# Revit family: 1-HC_RAS_HCL_TOSHIBA_TCTC_PAVPG_10-16
name_source: partatom
category: Mechanical Equipment
revit_build: Autodesk Revit 2017 (Build: 20160225_1515(x64)
units: mm (PartAtom-declared; Revit-internal decimal feet)

## family parameters
Always vertical = Yes
Cut with Voids When Loaded = No
OmniClass Number = 23.75.00.00
OmniClass Title = Climate Control (HVAC)
Part Type = Normal
Room Calculation Point = No
Round Connector Dimension = Use Diameter
Shared = No
Work Plane-Based = No

## types (4) — shared parameters
Compressor Type = Hermetic DC rotary compressor
Compressor detail - Motor output  (kW) = -
Content Supplier URL = www.hcltech.com
Custom = No
Depth (mm) = 300 mm
Drain pipe = -
Duct diameters = -
EMCS = 4
ETIM Article Class = EC001213
Frequency (Hz) = 50Hz
Height (mm) = 630 mm  [stored 2.06693 ft]
Hydronic Supply Diameter (mm) = 6 mm  [stored 0.019685 ft]
MCA (A) = -
MEPcontent Class = HEATPUMP
MOCP (A) = 15
Manufacturer = Toshiba
Manufacturer URL = https://www.toshiba-carrier.co.jp
Operating range - Cooling (°C) = -15 - 46
Operating range - Heating (°C) = -15 - 24
Product Line = TCTC
Red = Colour RGB-250 000 000
Refrigerant information = R32
Revit Version = 2017
Sound pressure dB(A) Cooling/Heating- Low = -
Sound pressure dB(A) Cooling/Heating- Low+ = -
Sound pressure dB(A) Cooling/Heating- Mid = -
Sound pressure dB(A) Cooling/Heating- Mid+ = -
Static pressure = -
URL = https://www.toshiba-carrier.co.jp
Voltage (V) = 220-240V
White = Colour RGB-255 255 255
Width (mm) = 800 mm  [stored 2.62467 ft]

## per-type parameters (varying)
| type | Air filter | Airflow m3/h- Cooling/Heating | Article Description | Description | Energy class | Hydronic Return Diameter (mm) | Pdesigh | Power consumption-Cooling (Kw) | Power consumption-Heating (Kw) | Rated Capacity kW - Cooling/Heating | Rated Power Consumption kW - Cooling/Heating | Rated efficiency - EER / COP | Running current-Cooling (A) | Running current-Heating (A) | Seasonal efficiency - SEER  / SCOP | Sound pressure dB(A) Cooling/Heating- High | Starting current | Weight (Kg) |
| RAS-10PAVPG-E | Plasma ion charger filtration | - | R32 DSK 9 | R32 DSK 9 | A+++ / A+++ | 10 mm  [stored 0.0328084 ft] | 2.5 / 3.0 (Tbiv= -7degC) | 425 | 570 | 2.5 / 3.2 | 0.45 / 0.60 | 5.56 / 5.33 | 2.31 - 2.13 | 3.12 - 2.86 | 10.6 / 5.20 | 46 / 47 |  | 38 |
| RAS-13PAVPG-E | - | - | R32 DSK 9 | R32 DSK 9 | A+++ / A+++ | 10 mm  [stored 0.0328084 ft] | 3.5 / 3.6 (Tbiv= -7degC) | 725 | 770 | 3.5 / 4.0 | 0.75 / 0.80 | 4.67 / 5.00 | 3.43 - 3.15 | 3.73 - 3.39 | 9.50 / 5.10 | 48 / 50 | - | 38 |
| RAS-16PAVPG-E | - | - | R32 DSK 9 | R32 DSK 9 | A+++ / A+++ | 13 mm | 4.5 / 4.5 (Tbiv= -7degC) | 1055 | 1340 | 4.5 / 5.5 | 1.08 / 1.37 | 4.17 / 4.01 | 5.05 - 4.64 | 6.16 - 5.63 | 8.50 / 4.60 | 49 / 50 | 6.44 - 5.89 | 38 |
| RAS-24PAVSG-E | - | 2916 /  2916 | R32 SHORAI | R32 SHORAI | A++ / A+ | 13 mm | 7.0 / 6.3 (Tbiv= -7degC) | 43 | 2367 | 7.0 / 8.0 | 2.25 / 2.41 | 3.11 / 3.32 | 0.38 - 0.35 | 10.02 - 9.95 | 6.2 / 4.0 | 53 / 53 | 10.8 | 41 |

note: column(s) folded — value = type name in every type: Article Type, Manufacturer Art. No., Model

note: [stored X ft] marks values corroborated as IEEE doubles in the binary element streams (Revit-internal decimal feet)

## geometry (parser evidence)
native form markers: Sweep x7
no freeform markers — native parametric forms only
